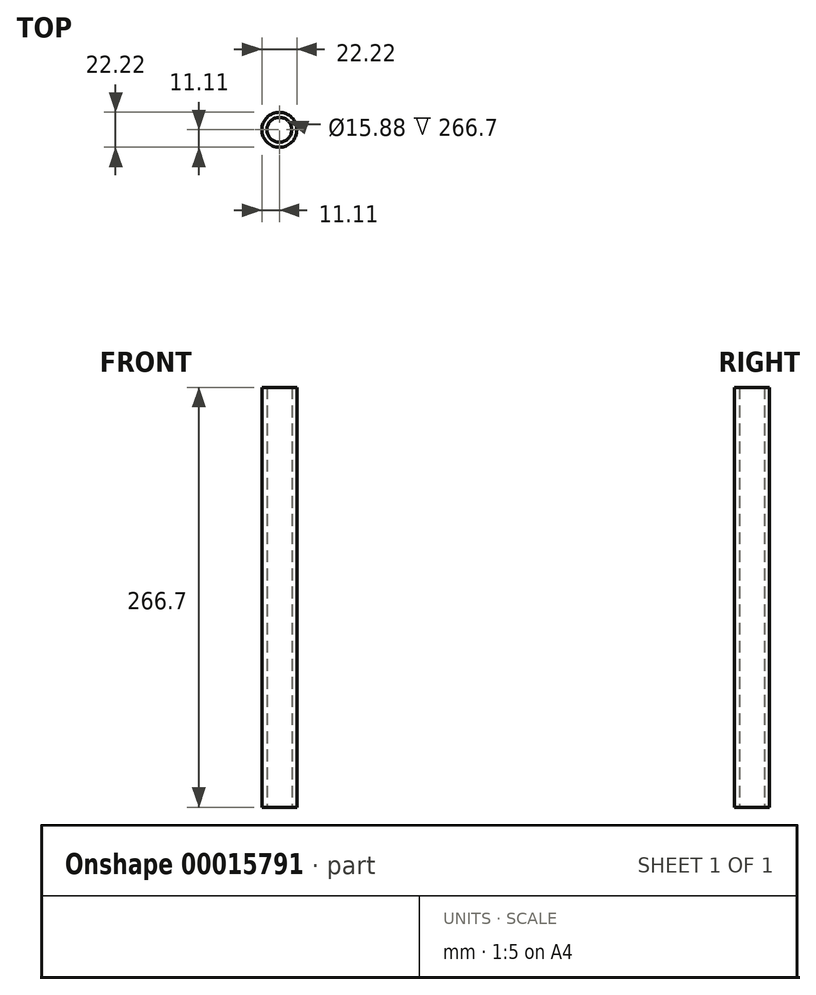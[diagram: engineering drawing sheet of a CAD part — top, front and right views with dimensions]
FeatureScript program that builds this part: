
annotation { "Feature Type Name" : "Feature", "Feature Type Description" : "" }
export const myFeature = defineFeature(function(context is Context, id is Id, definition is map)
    precondition{}
    {
        {
            var Q0;
            Q0=qCreatedBy(makeId("Top.planeOp"),FACE);
            var sketch = newSketch(context, id + "F0", { "sketchPlane" : qUnion([Q0])});
            skCircle(sketch, "E0", {"center": v(0, 0) * mm, "radius": 11.11 * mm});
            skCircle(sketch, "E1", {"center": v(0, 0) * mm, "radius": 7.94 * mm});
            skSolve(sketch);
        }
        {
            var Q0;
            Q0 = qSketchRegion(id + "F0", true);
            extrude(context, id + "F1", {"entities" : qUnion([Q0]), "depth" : 266.7 * mm});
        }
    });
